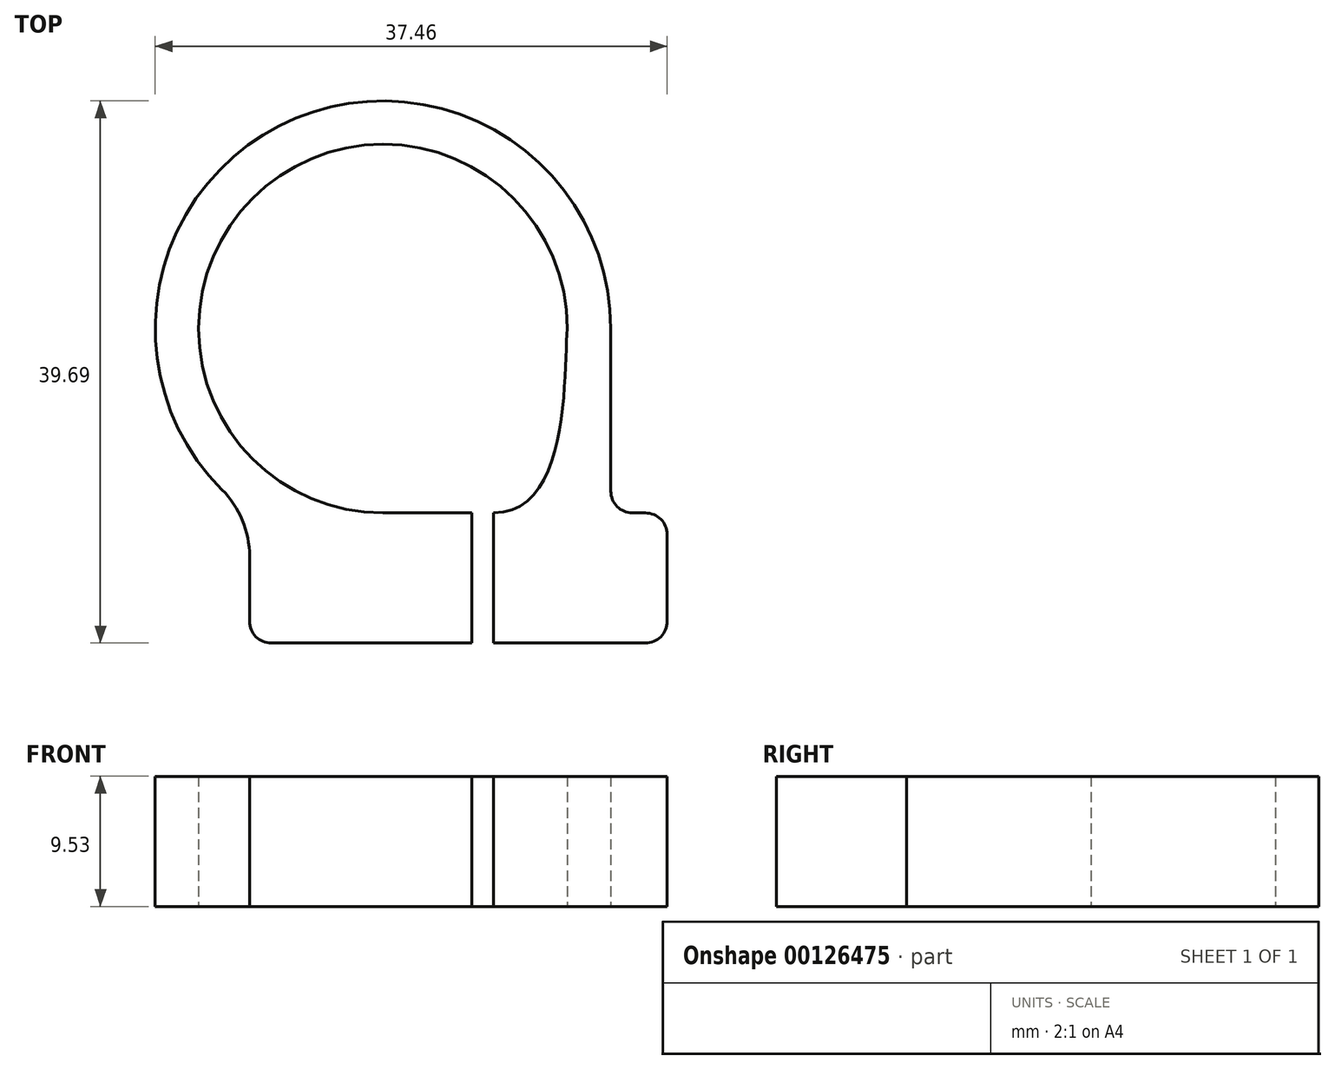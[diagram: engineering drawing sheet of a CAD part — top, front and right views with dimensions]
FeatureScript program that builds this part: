
annotation { "Feature Type Name" : "Feature", "Feature Type Description" : "" }
export const myFeature = defineFeature(function(context is Context, id is Id, definition is map)
    precondition{}
    {
        {
            var Q0;
            Q0=qCreatedBy(makeId("Top.planeOp"),FACE);
            var sketch = newSketch(context, id + "F0", { "sketchPlane" : qUnion([Q0])});
            skCircle(sketch, "E0", {"center": v(0, 0) * mm, "radius": 12.7 * mm, "construction": true});
            skCircle(sketch, "E1", {"center": v(0, 0) * mm, "radius": 13.5 * mm, "construction": true});
            skPoint(sketch, "E2", {"position": v(0, -12.7) * mm});
            skCircle(sketch, "E3", {"center": v(0, 0) * mm, "radius": 16.67 * mm, "construction": true});
            skPoint(sketch, "E4", {"position": v(0, 16.67) * mm});
            skLineSegment(sketch, "E5", {"start": v(0, 0) * mm, "end": v(0, 16.67) * mm, "construction": true});
            skLineSegment(sketch, "E6", {"start": v(-16.67, 0) * mm, "end": v(16.67, 0) * mm, "construction": true});
            skLineSegment(sketch, "E7", {"start": v(0, 0) * mm, "end": v(0, -12.7) * mm, "construction": true});
            skLineSegment(sketch, "E8", {"start": v(0, 0) * mm, "end": v(-11.79, -11.79) * mm, "construction": true});
            skLineSegment(sketch, "E9", {"start": v(0, -13.5) * mm, "end": v(26.57, -13.5) * mm, "construction": true});
            skLineSegment(sketch, "E10", {"start": v(0, -13.5) * mm, "end": v(-25.18, -13.5) * mm, "construction": true});
            skPoint(sketch, "E11", {"position": v(12.7, 0) * mm});
            skPoint(sketch, "E12", {"position": v(13.5, 0) * mm});
            skPoint(sketch, "E13", {"position": v(16.67, 0) * mm});
            skPoint(sketch, "E14", {"position": v(-9.54, -9.54) * mm});
            skArc(sketch, "E15", {"start": v(13.5, 0) * mm, "mid": v(-9.54, 9.54) * mm, "end": v(0, -13.5) * mm});
            skArc(sketch, "E16", {"start": v(16.67, 0) * mm, "mid": v(-6.38, 15.4) * mm, "end": v(-11.79, -11.79) * mm});
            skArc(sketch, "E17", {"start": v(-9.76, -16.67) * mm, "mid": v(-10.29, -14.03) * mm, "end": v(-11.79, -11.79) * mm});
            skLineSegment(sketch, "E18", {"start": v(0, -16.67) * mm, "end": v(-25.37, -16.67) * mm, "construction": true});
            skLineSegment(sketch, "E19", {"start": v(0, -13.5) * mm, "end": v(6.5, -13.5) * mm});
            skLineSegment(sketch, "E20", {"start": v(6.5, -13.5) * mm, "end": v(6.5, -23.02) * mm});
            skLineSegment(sketch, "E21", {"start": v(6.5, -23.02) * mm, "end": v(-8.18, -23.02) * mm});
            skLineSegment(sketch, "E22", {"start": v(-9.76, -16.67) * mm, "end": v(-9.76, -21.43) * mm});
            skLineSegment(sketch, "E23.bottom", {"start": v(6.5, -23.02) * mm, "end": v(8.1, -23.02) * mm, "construction": true});
            skLineSegment(sketch, "E23.top", {"start": v(6.5, -13.5) * mm, "end": v(8.1, -13.5) * mm, "construction": true});
            skLineSegment(sketch, "E23.left", {"start": v(6.5, -23.02) * mm, "end": v(6.5, -13.5) * mm});
            skLineSegment(sketch, "E23.right", {"start": v(8.1, -23.02) * mm, "end": v(8.1, -13.5) * mm, "construction": true});
            skFitSpline(sketch, "E24", {"points": [v(8.1, -13.5) * mm, v(13.5, 0) * mm], "startDerivative": vector(17.32, 0) * mm, "endDerivative": vector(0.93, 8.65) * mm});
            skLineSegment(sketch, "E25.bottom", {"start": v(8.1, -23.02) * mm, "end": v(19.2, -23.02) * mm});
            skLineSegment(sketch, "E25.left", {"start": v(8.1, -23.02) * mm, "end": v(8.1, -13.5) * mm});
            skLineSegment(sketch, "E25.right", {"start": v(20.8, -21.43) * mm, "end": v(20.8, -15.08) * mm});
            skLineSegment(sketch, "E26", {"start": v(16.67, 0) * mm, "end": v(16.67, -11.9) * mm});
            skLineSegment(sketch, "E27.trimOffspring", {"start": v(18.26, -13.5) * mm, "end": v(19.2, -13.5) * mm});
            skPoint(sketch, "E28.visualSharp", {"position": v(-9.76, -23.02) * mm});
            skArc(sketch, "E28.filletArc", {"start": v(-9.76, -21.43) * mm, "mid": v(-9.3, -22.55) * mm, "end": v(-8.18, -23.02) * mm});
            skPoint(sketch, "E29.visualSharp", {"position": v(20.8, -23.02) * mm});
            skArc(sketch, "E29.filletArc", {"start": v(19.2, -23.02) * mm, "mid": v(20.33, -22.55) * mm, "end": v(20.8, -21.43) * mm});
            skPoint(sketch, "E30.visualSharp", {"position": v(20.8, -13.5) * mm});
            skArc(sketch, "E31.filletArc", {"start": v(20.8, -15.08) * mm, "mid": v(20.33, -13.96) * mm, "end": v(19.2, -13.5) * mm});
            skPoint(sketch, "E32.visualSharp", {"position": v(16.67, -13.5) * mm});
            skArc(sketch, "E32.filletArc", {"start": v(16.67, -11.9) * mm, "mid": v(17.13, -13.03) * mm, "end": v(18.26, -13.5) * mm});
            skSolve(sketch);
        }
        {
            var Q0;
            Q0=makeQuery(id+"F0.imprint","IMPRINT",FACE,{"disambiguationData":[TD([[makeQuery(id+"F0.imprint","IMPRINT",EDGE,{"derivedFrom":sQuery(id+"F0.wireOp",EDGE,"E15")}),-1.0]])]});
            extrude(context, id + "F1", {"entities" : qUnion([Q0]), "depth" : 9.52 * mm});
        }
    });
